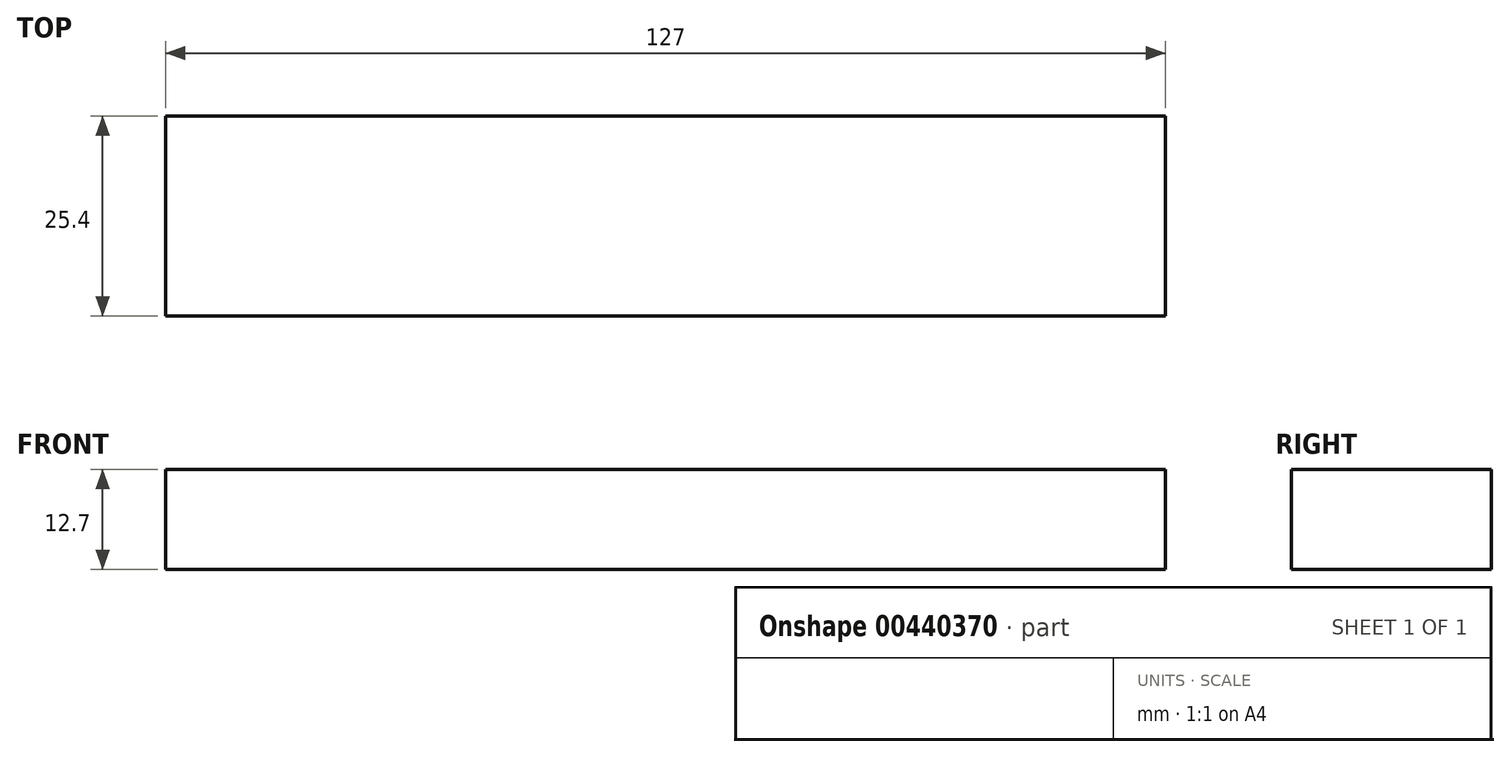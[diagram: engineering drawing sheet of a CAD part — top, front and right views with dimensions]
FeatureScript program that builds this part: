
annotation { "Feature Type Name" : "Feature", "Feature Type Description" : "" }
export const myFeature = defineFeature(function(context is Context, id is Id, definition is map)
    precondition{}
    {
        {
            var Q0;
            Q0=qCreatedBy(makeId("Front.planeOp"),FACE);
            var sketch = newSketch(context, id + "F0", { "sketchPlane" : qUnion([Q0])});
            skLineSegment(sketch, "E0.bottom", {"start": v(-63.5, -25.4) * mm, "end": v(63.5, -25.4) * mm});
            skLineSegment(sketch, "E0.top", {"start": v(-63.5, -38.1) * mm, "end": v(63.5, -38.1) * mm});
            skLineSegment(sketch, "E0.left", {"start": v(-63.5, -25.4) * mm, "end": v(-63.5, -38.1) * mm});
            skLineSegment(sketch, "E0.right", {"start": v(63.5, -25.4) * mm, "end": v(63.5, -38.1) * mm});
            skPoint(sketch, "E0.middle", {"position": v(0, -31.75) * mm});
            skLineSegment(sketch, "E1.bottom", {"start": v(-38.1, -25.4) * mm, "end": v(38.1, -25.4) * mm});
            skLineSegment(sketch, "E1.top", {"start": v(-31.75, 25.4) * mm, "end": v(31.75, 25.4) * mm});
            skLineSegment(sketch, "E1.left", {"start": v(-38.1, -25.4) * mm, "end": v(-38.1, 19.05) * mm});
            skLineSegment(sketch, "E1.right", {"start": v(38.1, -25.4) * mm, "end": v(38.1, 19.05) * mm});
            skPoint(sketch, "E1.middle", {"position": v(0, 0) * mm});
            skPoint(sketch, "E2.visualSharp", {"position": v(-38.1, 25.4) * mm});
            skArc(sketch, "E2.filletArc", {"start": v(-31.75, 25.4) * mm, "mid": v(-36.24, 23.54) * mm, "end": v(-38.1, 19.05) * mm});
            skPoint(sketch, "E3.visualSharp", {"position": v(38.1, 25.4) * mm});
            skArc(sketch, "E3.filletArc", {"start": v(38.1, 19.05) * mm, "mid": v(36.24, 23.54) * mm, "end": v(31.75, 25.4) * mm});
            skCircle(sketch, "E4", {"center": v(0, 0) * mm, "radius": 12.7 * mm});
            skSolve(sketch);
        }
        {
            var Q0;
            Q0=makeQuery(id+"F0.imprint","IMPRINT",FACE,{"disambiguationData":[TD([[makeQuery(id+"F0.imprint","IMPRINT",EDGE,{"derivedFrom":sQuery(id+"F0.wireOp",EDGE,"E1.bottom")}),1.0]])]});
            var Q1;
            Q1=makeQuery(id+"F0.imprint","IMPRINT",FACE,{"disambiguationData":[TD([[makeQuery(id+"F0.imprint","IMPRINT",EDGE,{"derivedFrom":sQuery(id+"F0.wireOp",EDGE,"E0.top")}),1.0]])]});
            extrude(context, id + "F1", {"entities" : qUnion([Q0, Q1]), "endBound" : BoundingType.SYMMETRIC, "depth" : 25.4 * mm});
        }
    });
